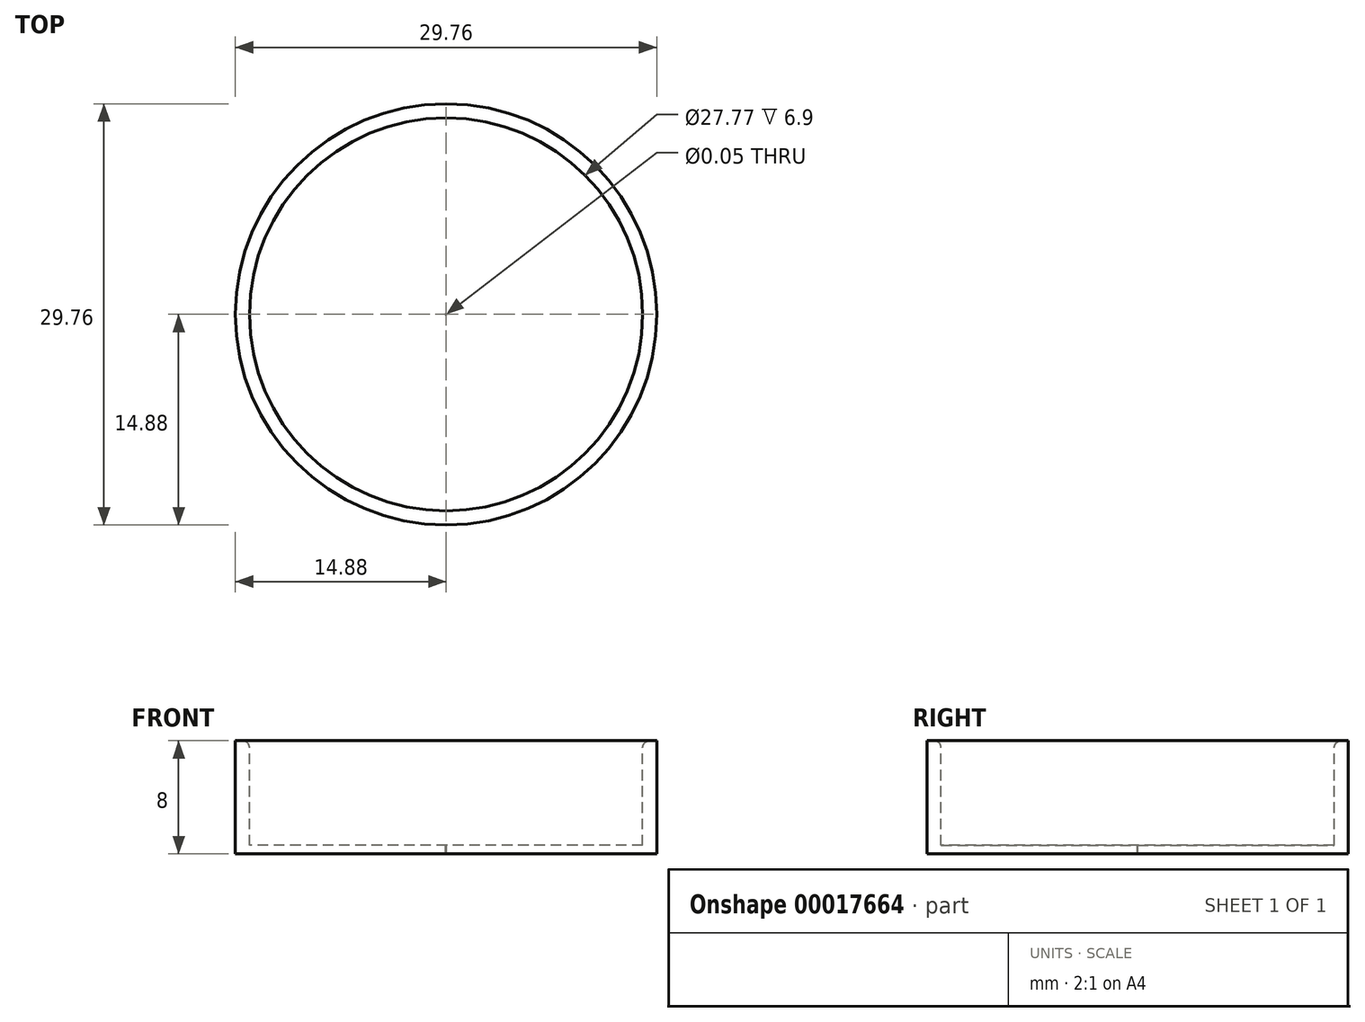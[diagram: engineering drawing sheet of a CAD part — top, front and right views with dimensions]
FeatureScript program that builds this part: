
annotation { "Feature Type Name" : "Feature", "Feature Type Description" : "" }
export const myFeature = defineFeature(function(context is Context, id is Id, definition is map)
    precondition{}
    {
        {
            var Q0;
            Q0=qCreatedBy(makeId("Front.planeOp"),FACE);
            var sketch = newSketch(context, id + "F0", { "sketchPlane" : qUnion([Q0])});
            skLineSegment(sketch, "E0", {"start": v(0, 23.42) * mm, "end": v(0, -24.67) * mm});
            skSolve(sketch);
        }
        {
            var Q0;
            Q0=qCreatedBy(makeId("Front.planeOp"),FACE);
            var sketch = newSketch(context, id + "F1", { "sketchPlane" : qUnion([Q0])});
            skLineSegment(sketch, "E1", {"start": v(13.88, 8) * mm, "end": v(13.88, 0.6) * mm});
            skLineSegment(sketch, "E2", {"start": v(13.88, 0.6) * mm, "end": v(0.02, 0.6) * mm});
            skLineSegment(sketch, "E3", {"start": v(0.02, 0.6) * mm, "end": v(0.02, 0) * mm});
            skLineSegment(sketch, "E4", {"start": v(0.02, 0) * mm, "end": v(14.88, 0) * mm});
            skLineSegment(sketch, "E5", {"start": v(14.88, 0) * mm, "end": v(14.88, 8) * mm});
            skLineSegment(sketch, "E6", {"start": v(14.88, 8) * mm, "end": v(13.88, 8) * mm});
            skSolve(sketch);
        }
        {
            var Q0;
            Q0=makeQuery(id+"F1.imprint","IMPRINT",FACE,{"disambiguationData":[TD([[makeQuery(id+"F1.imprint","IMPRINT",EDGE,{"derivedFrom":sQuery(id+"F1.wireOp",EDGE,"E1")}),1.0]])]});
            var Q1;
            Q1=sQuery(id+"F0.wireOp",EDGE,"E0");
            revolve(context, id + "F2", {"entities" : qUnion([Q0]), "axis" : qUnion([Q1]), "revolveType" : RevolveType.FULL});
        }
        {
            var Q0;
            Q0=makeQuery(id+"F2.opRevolve","SWEPT_EDGE",EDGE,{"disambiguationData":[OSD([sQuery(id+"F1.wireOp",EDGE,"E1"),sQuery(id+"F1.wireOp",EDGE,"E6")])]});
            fillet(context, id + "F3", {"entities" : qUnion([Q0]), "radius" : 0.5 * mm, "allowEdgeOverflow" : false});
        }
    });
